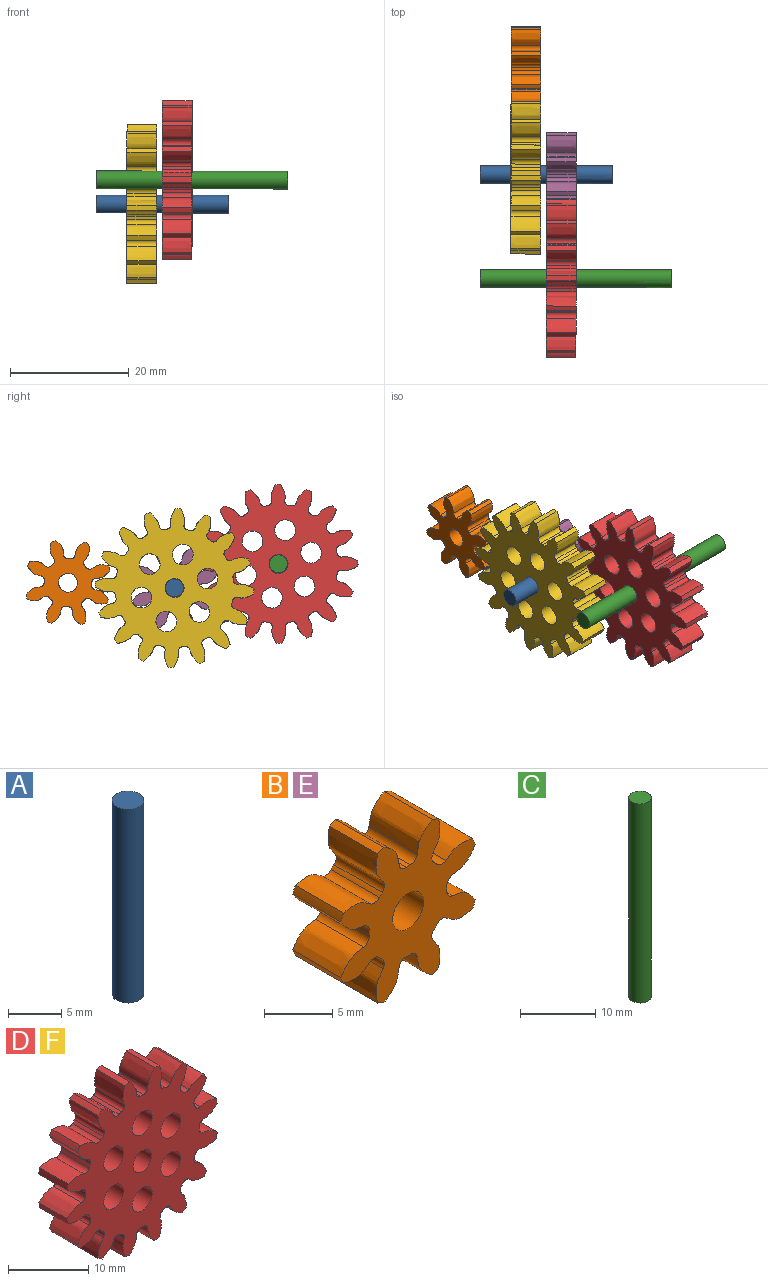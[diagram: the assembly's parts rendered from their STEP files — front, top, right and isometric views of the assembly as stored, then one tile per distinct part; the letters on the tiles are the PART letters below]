
ASSEMBLY  parts=6 mates=3
PART A: 3 faces, bbox 3x3x22.4 mm
  f0: cylinder r=1.5mm len=22.35mm, axis (0,0,-1), area 210.6mm2, adj f1,f2
  f1: plane 3x3mm, normal (0,0,1), area 7.1mm2, adj f0
  f2: plane 3x3mm, normal (0,0,-1), area 7.1mm2, adj f0
PART B: 51 faces, bbox 15x6.1x15 mm
  f0: cylinder r=7.4mm len=5mm, axis (0,1,0), area 3.5mm2, adj f7,f10,f41,f48
  f1: cylinder r=7.4mm len=5mm, axis (0,1,0), area 3.5mm2, adj f7,f10,f36,f43
  f2: cylinder r=7.4mm len=5mm, axis (0,1,0), area 3.5mm2, adj f7,f10,f31,f38
  f3: cylinder r=7.4mm len=5mm, axis (0,1,0), area 3.5mm2, adj f7,f10,f26,f33
  f4: cylinder r=7.4mm len=5mm, axis (0,1,0), area 3.5mm2, adj f7,f10,f21,f28
  f5: cylinder r=7.4mm len=5mm, axis (0,1,0), area 3.5mm2, adj f7,f10,f16,f23
  f6: cylinder r=7.4mm len=5mm, axis (0,1,0), area 3.5mm2, adj f7,f10,f11,f18
  f7: plane 15.02x15.02mm, normal (0,-1,0), area 92mm2, adj f0,f1,f2,f3,f4,f5,f6,f8
  f8: cylinder r=1.6mm len=5mm, axis (0,1,0), area 50.3mm2, adj f7,f10
  f9: cylinder r=7.4mm len=5mm, axis (0,1,0), area 3.5mm2, adj f7,f10,f13,f46
  f10: plane 15.02x15.02mm, normal (0,1,0), area 92mm2, adj f0,f1,f2,f3,f4,f5,f6,f8
  f11: extruded ~5x2.37mm, area 14.8mm2, adj f6,f7,f10,f14
  f12: cylinder r=4.03mm len=5mm, axis (0,1,0), area 2.1mm2, adj f7,f10,f14,f15
  f13: extruded ~5x2.37mm, area 14.8mm2, adj f7,f9,f10,f15
  f14: cylinder r=0.7mm len=5mm, axis (0,1,0), area 5.1mm2, adj f7,f10,f11,f12
  f15: cylinder r=0.7mm len=5mm, axis (0,1,0), area 5.1mm2, adj f7,f10,f12,f13
  f16: extruded ~5x2.78mm, area 14.8mm2, adj f5,f7,f10,f19
  f17: cylinder r=4.03mm len=5mm, axis (0,1,0), area 2.1mm2, adj f7,f10,f19,f20
  f18: extruded ~5x2.78mm, area 14.8mm2, adj f6,f7,f10,f20
  f19: cylinder r=0.7mm len=5mm, axis (0,1,0), area 5.1mm2, adj f7,f10,f16,f17
  f20: cylinder r=0.7mm len=5mm, axis (0,1,0), area 5.1mm2, adj f7,f10,f17,f18
  f21: extruded ~5x2.37mm, area 14.8mm2, adj f4,f7,f10,f24
  f22: cylinder r=4.03mm len=5mm, axis (0,1,0), area 2.1mm2, adj f7,f10,f24,f25
  f23: extruded ~5x2.37mm, area 14.8mm2, adj f5,f7,f10,f25
  f24: cylinder r=0.7mm len=5mm, axis (0,1,0), area 5.1mm2, adj f7,f10,f21,f22
  f25: cylinder r=0.7mm len=5mm, axis (0,1,0), area 5.1mm2, adj f7,f10,f22,f23
  f26: extruded ~5x2.78mm, area 14.8mm2, adj f3,f7,f10,f29
  f27: cylinder r=4.03mm len=5mm, axis (0,1,0), area 2.1mm2, adj f7,f10,f29,f30
  f28: extruded ~5x2.78mm, area 14.8mm2, adj f4,f7,f10,f30
  f29: cylinder r=0.7mm len=5mm, axis (0,1,0), area 5.1mm2, adj f7,f10,f26,f27
  f30: cylinder r=0.7mm len=5mm, axis (0,1,0), area 5.1mm2, adj f7,f10,f27,f28
  f31: extruded ~5x2.37mm, area 14.8mm2, adj f2,f7,f10,f34
  f32: cylinder r=4.03mm len=5mm, axis (0,1,0), area 2.1mm2, adj f7,f10,f34,f35
  f33: extruded ~5x2.37mm, area 14.8mm2, adj f3,f7,f10,f35
  f34: cylinder r=0.7mm len=5mm, axis (0,1,0), area 5.1mm2, adj f7,f10,f31,f32
  f35: cylinder r=0.7mm len=5mm, axis (0,1,0), area 5.1mm2, adj f7,f10,f32,f33
  f36: extruded ~5x2.78mm, area 14.8mm2, adj f1,f7,f10,f39
  f37: cylinder r=4.03mm len=5mm, axis (0,1,0), area 2.1mm2, adj f7,f10,f39,f40
  f38: extruded ~5x2.78mm, area 14.8mm2, adj f2,f7,f10,f40
  f39: cylinder r=0.7mm len=5mm, axis (0,1,0), area 5.1mm2, adj f7,f10,f36,f37
  f40: cylinder r=0.7mm len=5mm, axis (0,1,0), area 5.1mm2, adj f7,f10,f37,f38
  f41: extruded ~5x2.37mm, area 14.8mm2, adj f0,f7,f10,f44
  f42: cylinder r=4.03mm len=5mm, axis (0,1,0), area 2.1mm2, adj f7,f10,f44,f45
  f43: extruded ~5x2.37mm, area 14.8mm2, adj f1,f7,f10,f45
  f44: cylinder r=0.7mm len=5mm, axis (0,1,0), area 5.1mm2, adj f7,f10,f41,f42
  f45: cylinder r=0.7mm len=5mm, axis (0,1,0), area 5.1mm2, adj f7,f10,f42,f43
  f46: extruded ~5x2.78mm, area 14.8mm2, adj f7,f9,f10,f49
  f47: cylinder r=4.03mm len=5mm, axis (0,1,0), area 2.1mm2, adj f7,f10,f49,f50
  f48: extruded ~5x2.78mm, area 14.8mm2, adj f0,f7,f10,f50
  f49: cylinder r=0.7mm len=5mm, axis (0,1,0), area 5.1mm2, adj f7,f10,f46,f47
  f50: cylinder r=0.7mm len=5mm, axis (0,1,0), area 5.1mm2, adj f7,f10,f47,f48
PART C: 3 faces, bbox 3x3x32.4 mm
  f0: cylinder r=1.5mm len=32.35mm, axis (0,0,-1), area 304.9mm2, adj f1,f2
  f1: plane 3x3mm, normal (0,0,1), area 7.1mm2, adj f0
  f2: plane 3x3mm, normal (0,0,-1), area 7.1mm2, adj f0
PART D: 105 faces, bbox 26.9x5.5x26.9 mm
  f0: cylinder r=13.4mm len=5mm, axis (0,1,0), area 4.4mm2, adj f15,f18,f89,f96
  f1: cylinder r=13.4mm len=5mm, axis (0,1,0), area 4.4mm2, adj f15,f18,f64,f91
  f2: cylinder r=13.4mm len=5mm, axis (0,1,0), area 4.4mm2, adj f15,f18,f86,f94
  f3: cylinder r=13.4mm len=5mm, axis (0,1,0), area 4.4mm2, adj f15,f18,f74,f81
  f4: cylinder r=13.4mm len=5mm, axis (0,1,0), area 4.4mm2, adj f15,f18,f44,f76
  f5: cylinder r=13.4mm len=5mm, axis (0,1,0), area 4.4mm2, adj f15,f18,f71,f79
  f6: cylinder r=13.4mm len=5mm, axis (0,1,0), area 4.4mm2, adj f15,f18,f66,f69
  f7: cylinder r=13.4mm len=5mm, axis (0,1,0), area 4.4mm2, adj f15,f18,f54,f61
  f8: cylinder r=13.4mm len=5mm, axis (0,1,0), area 4.4mm2, adj f15,f18,f24,f56
  f9: cylinder r=13.4mm len=5mm, axis (0,1,0), area 4.4mm2, adj f15,f18,f51,f59
  f10: cylinder r=13.4mm len=5mm, axis (0,1,0), area 4.4mm2, adj f15,f18,f46,f49
  f11: cylinder r=13.4mm len=5mm, axis (0,1,0), area 4.4mm2, adj f15,f18,f34,f41
  f12: cylinder r=13.4mm len=5mm, axis (0,1,0), area 4.4mm2, adj f15,f18,f19,f36
  f13: cylinder r=13.4mm len=5mm, axis (0,1,0), area 4.4mm2, adj f15,f18,f31,f39
  f14: cylinder r=13.4mm len=5mm, axis (0,1,0), area 4.4mm2, adj f15,f18,f26,f29
  f15: plane 26.95x26.95mm, normal (0,-1,0), area 359.6mm2, adj f0,f1,f2,f3,f4,f5,f6,f7
  f16: cylinder r=1.6mm len=5mm, axis (0,1,0), area 50.3mm2, adj f15,f18
  f17: cylinder r=13.4mm len=5mm, axis (0,1,0), area 4.4mm2, adj f15,f18,f21,f84
  f18: plane 26.95x26.95mm, normal (0,1,0), area 359.6mm2, adj f0,f1,f2,f3,f4,f5,f6,f7
  f19: extruded ~5x2.55mm, area 14.5mm2, adj f12,f15,f18,f22
  f20: cylinder r=10.02mm len=5mm, axis (0,1,0), area 2.6mm2, adj f15,f18,f22,f23
  f21: extruded ~5x2.55mm, area 14.5mm2, adj f15,f17,f18,f23
  f22: cylinder r=0.71mm len=5mm, axis (0,1,0), area 5.4mm2, adj f15,f18,f19,f20
  f23: cylinder r=0.71mm len=5mm, axis (0,1,0), area 5.4mm2, adj f15,f18,f20,f21
  f24: extruded ~5x2.55mm, area 14.5mm2, adj f8,f15,f18,f27
  f25: cylinder r=10.02mm len=5mm, axis (0,1,0), area 2.6mm2, adj f15,f18,f27,f28
  f26: extruded ~5x2.55mm, area 14.5mm2, adj f14,f15,f18,f28
  f27: cylinder r=0.71mm len=5mm, axis (0,1,0), area 5.4mm2, adj f15,f18,f24,f25
  f28: cylinder r=0.71mm len=5mm, axis (0,1,0), area 5.4mm2, adj f15,f18,f25,f26
  f29: extruded ~5x2.81mm, area 14.5mm2, adj f14,f15,f18,f32
  f30: cylinder r=10.02mm len=5mm, axis (0,1,0), area 2.6mm2, adj f15,f18,f32,f33
  f31: extruded ~5x2.07mm, area 14.5mm2, adj f13,f15,f18,f33
  f32: cylinder r=0.71mm len=5mm, axis (0,1,0), area 5.4mm2, adj f15,f18,f29,f30
  f33: cylinder r=0.71mm len=5mm, axis (0,1,0), area 5.4mm2, adj f15,f18,f30,f31
  f34: extruded ~5x2.07mm, area 14.5mm2, adj f11,f15,f18,f37
  f35: cylinder r=10.02mm len=5mm, axis (0,1,0), area 2.6mm2, adj f15,f18,f37,f38
  f36: extruded ~5x2.81mm, area 14.5mm2, adj f12,f15,f18,f38
  f37: cylinder r=0.71mm len=5mm, axis (0,1,0), area 5.4mm2, adj f15,f18,f34,f35
  f38: cylinder r=0.71mm len=5mm, axis (0,1,0), area 5.4mm2, adj f15,f18,f35,f36
  f39: extruded ~5x2.64mm, area 14.5mm2, adj f13,f15,f18,f42
  f40: cylinder r=10.02mm len=5mm, axis (0,1,0), area 2.6mm2, adj f15,f18,f42,f43
  f41: extruded ~5x2.64mm, area 14.5mm2, adj f11,f15,f18,f43
  f42: cylinder r=0.71mm len=5mm, axis (0,1,0), area 5.4mm2, adj f15,f18,f39,f40
  f43: cylinder r=0.71mm len=5mm, axis (0,1,0), area 5.4mm2, adj f15,f18,f40,f41
  f44: extruded ~5x2.55mm, area 14.5mm2, adj f4,f15,f18,f47
  f45: cylinder r=10.02mm len=5mm, axis (0,1,0), area 2.6mm2, adj f15,f18,f47,f48
  f46: extruded ~5x2.55mm, area 14.5mm2, adj f10,f15,f18,f48
  f47: cylinder r=0.71mm len=5mm, axis (0,1,0), area 5.4mm2, adj f15,f18,f44,f45
  f48: cylinder r=0.71mm len=5mm, axis (0,1,0), area 5.4mm2, adj f15,f18,f45,f46
  f49: extruded ~5x2.81mm, area 14.5mm2, adj f10,f15,f18,f52
  f50: cylinder r=10.02mm len=5mm, axis (0,1,0), area 2.6mm2, adj f15,f18,f52,f53
  f51: extruded ~5x2.07mm, area 14.5mm2, adj f9,f15,f18,f53
  f52: cylinder r=0.71mm len=5mm, axis (0,1,0), area 5.4mm2, adj f15,f18,f49,f50
  f53: cylinder r=0.71mm len=5mm, axis (0,1,0), area 5.4mm2, adj f15,f18,f50,f51
  f54: extruded ~5x2.07mm, area 14.5mm2, adj f7,f15,f18,f57
  f55: cylinder r=10.02mm len=5mm, axis (0,1,0), area 2.6mm2, adj f15,f18,f57,f58
  f56: extruded ~5x2.81mm, area 14.5mm2, adj f8,f15,f18,f58
  f57: cylinder r=0.71mm len=5mm, axis (0,1,0), area 5.4mm2, adj f15,f18,f54,f55
  f58: cylinder r=0.71mm len=5mm, axis (0,1,0), area 5.4mm2, adj f15,f18,f55,f56
  f59: extruded ~5x2.64mm, area 14.5mm2, adj f9,f15,f18,f62
  f60: cylinder r=10.02mm len=5mm, axis (0,1,0), area 2.6mm2, adj f15,f18,f62,f63
  f61: extruded ~5x2.64mm, area 14.5mm2, adj f7,f15,f18,f63
  f62: cylinder r=0.71mm len=5mm, axis (0,1,0), area 5.4mm2, adj f15,f18,f59,f60
  f63: cylinder r=0.71mm len=5mm, axis (0,1,0), area 5.4mm2, adj f15,f18,f60,f61
  f64: extruded ~5x2.55mm, area 14.5mm2, adj f1,f15,f18,f67
  f65: cylinder r=10.02mm len=5mm, axis (0,1,0), area 2.6mm2, adj f15,f18,f67,f68
  f66: extruded ~5x2.55mm, area 14.5mm2, adj f6,f15,f18,f68
  f67: cylinder r=0.71mm len=5mm, axis (0,1,0), area 5.4mm2, adj f15,f18,f64,f65
  f68: cylinder r=0.71mm len=5mm, axis (0,1,0), area 5.4mm2, adj f15,f18,f65,f66
  f69: extruded ~5x2.81mm, area 14.5mm2, adj f6,f15,f18,f72
  f70: cylinder r=10.02mm len=5mm, axis (0,1,0), area 2.6mm2, adj f15,f18,f72,f73
  f71: extruded ~5x2.07mm, area 14.5mm2, adj f5,f15,f18,f73
  f72: cylinder r=0.71mm len=5mm, axis (0,1,0), area 5.4mm2, adj f15,f18,f69,f70
  f73: cylinder r=0.71mm len=5mm, axis (0,1,0), area 5.4mm2, adj f15,f18,f70,f71
  f74: extruded ~5x2.07mm, area 14.5mm2, adj f3,f15,f18,f77
  f75: cylinder r=10.02mm len=5mm, axis (0,1,0), area 2.6mm2, adj f15,f18,f77,f78
  f76: extruded ~5x2.81mm, area 14.5mm2, adj f4,f15,f18,f78
  f77: cylinder r=0.71mm len=5mm, axis (0,1,0), area 5.4mm2, adj f15,f18,f74,f75
  f78: cylinder r=0.71mm len=5mm, axis (0,1,0), area 5.4mm2, adj f15,f18,f75,f76
  f79: extruded ~5x2.64mm, area 14.5mm2, adj f5,f15,f18,f82
  f80: cylinder r=10.02mm len=5mm, axis (0,1,0), area 2.6mm2, adj f15,f18,f82,f83
  f81: extruded ~5x2.64mm, area 14.5mm2, adj f3,f15,f18,f83
  f82: cylinder r=0.71mm len=5mm, axis (0,1,0), area 5.4mm2, adj f15,f18,f79,f80
  f83: cylinder r=0.71mm len=5mm, axis (0,1,0), area 5.4mm2, adj f15,f18,f80,f81
  f84: extruded ~5x2.81mm, area 14.5mm2, adj f15,f17,f18,f87
  f85: cylinder r=10.02mm len=5mm, axis (0,1,0), area 2.6mm2, adj f15,f18,f87,f88
  f86: extruded ~5x2.07mm, area 14.5mm2, adj f2,f15,f18,f88
  f87: cylinder r=0.71mm len=5mm, axis (0,1,0), area 5.4mm2, adj f15,f18,f84,f85
  f88: cylinder r=0.71mm len=5mm, axis (0,1,0), area 5.4mm2, adj f15,f18,f85,f86
  f89: extruded ~5x2.07mm, area 14.5mm2, adj f0,f15,f18,f92
  f90: cylinder r=10.02mm len=5mm, axis (0,1,0), area 2.6mm2, adj f15,f18,f92,f93
  f91: extruded ~5x2.81mm, area 14.5mm2, adj f1,f15,f18,f93
  f92: cylinder r=0.71mm len=5mm, axis (0,1,0), area 5.4mm2, adj f15,f18,f89,f90
  f93: cylinder r=0.71mm len=5mm, axis (0,1,0), area 5.4mm2, adj f15,f18,f90,f91
  f94: extruded ~5x2.64mm, area 14.5mm2, adj f2,f15,f18,f97
  f95: cylinder r=10.02mm len=5mm, axis (0,1,0), area 2.6mm2, adj f15,f18,f97,f98
  f96: extruded ~5x2.64mm, area 14.5mm2, adj f0,f15,f18,f98
  f97: cylinder r=0.71mm len=5mm, axis (0,1,0), area 5.4mm2, adj f15,f18,f94,f95
  f98: cylinder r=0.71mm len=5mm, axis (0,1,0), area 5.4mm2, adj f15,f18,f95,f96
  f99: cylinder r=1.75mm len=5mm, axis (0,-1,0), area 55mm2, adj f15,f18
  f100: cylinder r=1.75mm len=5mm, axis (0,-1,0), area 55mm2, adj f15,f18
  f101: cylinder r=1.75mm len=5mm, axis (0,-1,0), area 55mm2, adj f15,f18
  f102: cylinder r=1.75mm len=5mm, axis (0,-1,0), area 55mm2, adj f15,f18
  f103: cylinder r=1.75mm len=5mm, axis (0,-1,0), area 55mm2, adj f15,f18
  f104: cylinder r=1.75mm len=5mm, axis (0,-1,0), area 55mm2, adj f15,f18
PART E: same geometry as B
PART F: same geometry as D
PLACE A rot(axis=(-0.57,-0.6,0.57),118.2deg) t=(92.98,-57.84,0.23)mm
PLACE B rot(axis=(0.03,-0.02,1),89.9deg) t=(75.84,-39.84,1.16)mm
PLACE C rot(axis=(-0.57,-0.6,0.57),118.2deg) t=(102.96,-75.39,4.29)mm
PLACE D rot(axis=(0.1,-0.09,0.99),90.4deg) t=(81.78,-75.35,4.33)mm
PLACE E rot(axis=(0.03,-0.02,1),89.9deg) t=(81.81,-57.82,0.25)mm
PLACE F rot(axis=(0.12,-0.12,0.99),90.7deg) t=(75.81,-57.81,0.26)mm
MATE fastened D.f0 <-> C.f0  axis (-1,0,0) through (81.78,-75.35,4.33)mm
MATE fastened F.f0 <-> A.f0  axis (-1,0,0) through (75.81,-57.81,0.26)mm
MATE fastened E.f0 <-> A.f0  axis (-1,0,0) through (81.81,-57.82,0.25)mm
